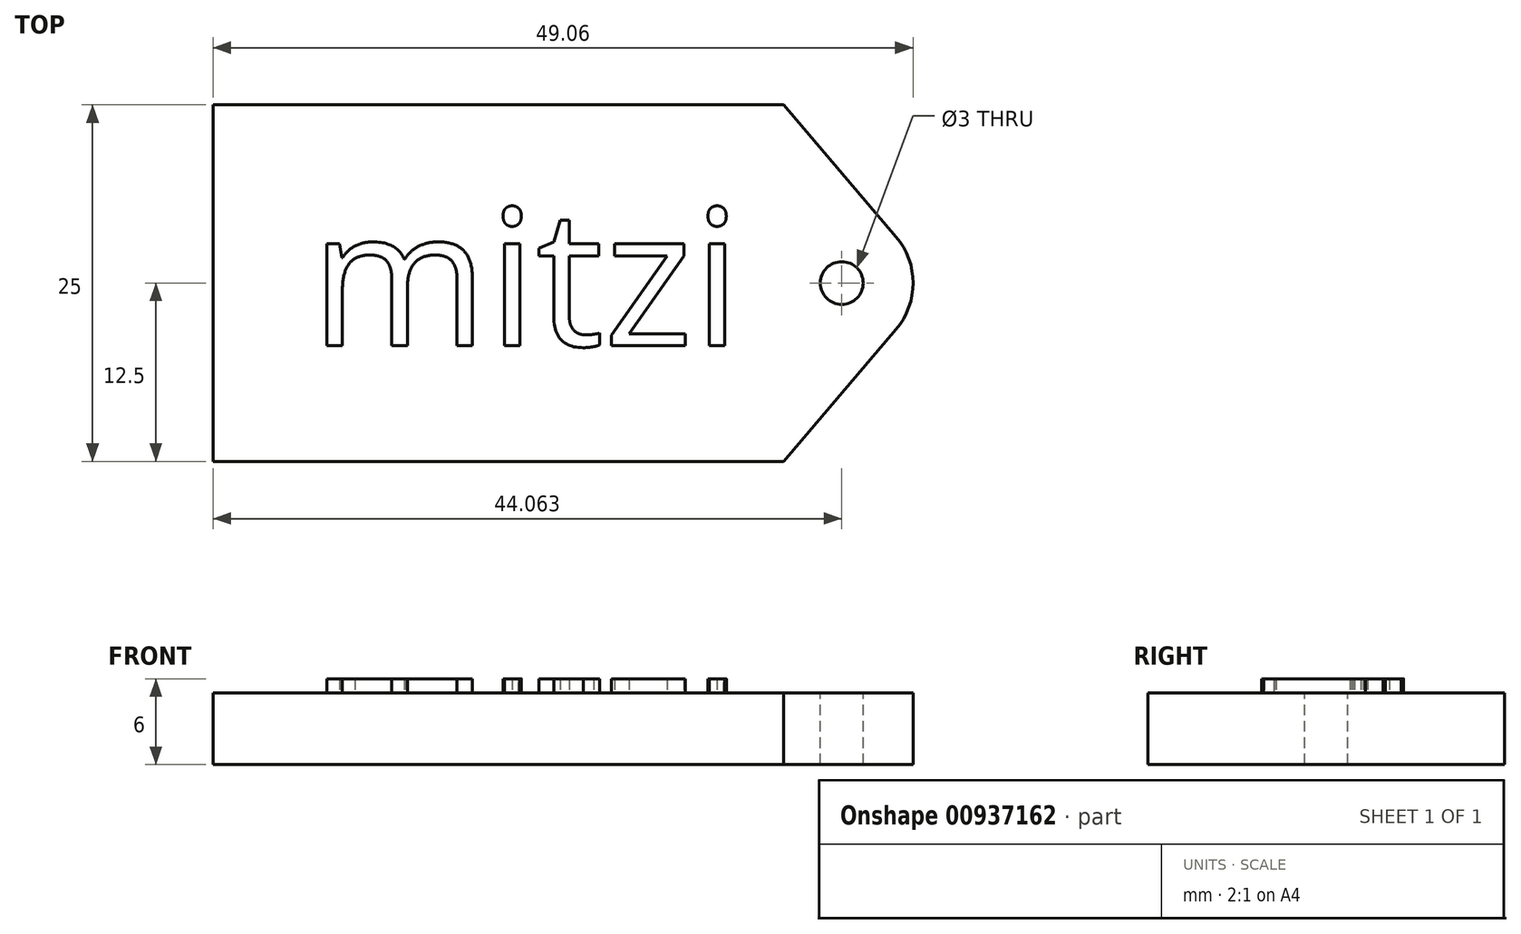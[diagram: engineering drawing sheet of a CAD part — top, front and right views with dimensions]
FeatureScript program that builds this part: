
annotation { "Feature Type Name" : "Feature", "Feature Type Description" : "" }
export const myFeature = defineFeature(function(context is Context, id is Id, definition is map)
    precondition{}
    {
        {
            var Q0;
            Q0=qCreatedBy(makeId("Top.planeOp"),FACE);
            var sketch = newSketch(context, id + "F0", { "sketchPlane" : qUnion([Q0])});
            skLineSegment(sketch, "E0.bottom", {"start": v(20, -12.5) * mm, "end": v(-20, -12.5) * mm});
            skLineSegment(sketch, "E0.top", {"start": v(20, 12.5) * mm, "end": v(-20, 12.5) * mm});
            skLineSegment(sketch, "E0.right", {"start": v(-20, -12.5) * mm, "end": v(-20, 12.5) * mm});
            skPoint(sketch, "E0.middle", {"position": v(0, 0) * mm});
            skPoint(sketch, "E1", {"position": v(30.63, 0) * mm});
            skLineSegment(sketch, "E2", {"start": v(20, 12.5) * mm, "end": v(30.63, 0) * mm});
            skLineSegment(sketch, "E3", {"start": v(20, -12.5) * mm, "end": v(30.63, 0) * mm});
            skSolve(sketch);
        }
        {
            var Q0;
            Q0 = qSketchRegion(id + "F0", true);
            extrude(context, id + "F1", {"entities" : qUnion([Q0]), "depth" : 5 * mm, "offsetDistance" : 25 * mm});
        }
        {
            var Q0;
            Q0=makeQuery(id+"F1.opExtrude","SWEPT_EDGE",EDGE,{"disambiguationData":[OSD([sQuery(id+"F0.wireOp",EDGE,"E2"),sQuery(id+"F0.wireOp",EDGE,"E3")])]});
            fillet(context, id + "F2", {"entities" : qUnion([Q0]), "radius" : 5 * mm, "tangentPropagation" : true, "allowEdgeOverflow" : false});
        }
        {
            var Q0;
            Q0=makeQuery(id+"F1.opExtrude","CAP_FACE",FACE,{"disambiguationData":[OSD([sQuery(id+"F0.wireOp",EDGE,"E0.bottom"),sQuery(id+"F0.wireOp",EDGE,"E0.top"),sQuery(id+"F0.wireOp",EDGE,"E0.right"),sQuery(id+"F0.wireOp",EDGE,"E2"),sQuery(id+"F0.wireOp",EDGE,"E3")])],"isStart":false});
            var sketch = newSketch(context, id + "F3", { "sketchPlane" : qUnion([Q0])});
            skPoint(sketch, "E4", {"position": v(0, 0) * mm});
            skPoint(sketch, "E5", {"position": v(24.06, 0) * mm});
            skSolve(sketch);
        }
        {
            var Q0;
            Q0=sQuery(id+"F3.wireOp",VERTEX,"E5");
            var Q1;
            Q1=makeQuery(id+"F1.opExtrude","SWEPT_BODY",BODY,{"disambiguationData":[OSD([sQuery(id+"F0.wireOp",EDGE,"E0.bottom"),sQuery(id+"F0.wireOp",EDGE,"E0.top"),sQuery(id+"F0.wireOp",EDGE,"E0.right"),sQuery(id+"F0.wireOp",EDGE,"E2"),sQuery(id+"F0.wireOp",EDGE,"E3")])]});
            hole(context, id + "F4", {"style" : HoleStyle.SIMPLE, "endStyle" : HoleEndStyle.THROUGH, "holeDiameter" : 3 * mm, "majorDiameter" : 5 * mm, "isTappedThrough" : true, "tappedDepth" : 12 * mm, "tapClearance" : 3, "locations" : qUnion([Q0]), "scope" : qUnion([Q1])});
        }
        {
            var Q0;
            Q0=makeQuery(id+"F1.opExtrude","CAP_FACE",FACE,{"disambiguationData":[OSD([sQuery(id+"F0.wireOp",EDGE,"E0.bottom"),sQuery(id+"F0.wireOp",EDGE,"E0.top"),sQuery(id+"F0.wireOp",EDGE,"E0.right"),sQuery(id+"F0.wireOp",EDGE,"E2"),sQuery(id+"F0.wireOp",EDGE,"E3")])],"isStart":false});
            var sketch = newSketch(context, id + "F5", { "sketchPlane" : qUnion([Q0])});
            skText(sketch, "E6", { "text": "mitzi", "fontName": "OpenSans-Regular.ttf"});
            const initialGuessF5  = {"E6": [-0.01317, -0.0044, 1, 0, 0.00963]};
            skSetInitialGuess(sketch, initialGuessF5);
            skSolve(sketch);
        }
        {
            var Q0;
            Q0 = qSketchRegion(id + "F5", true);
            extrude(context, id + "F6", {"entities" : qUnion([Q0]), "operationType" : NewBodyOperationType.ADD, "depth" : 1 * mm, "offsetDistance" : 25 * mm});
        }
    });
